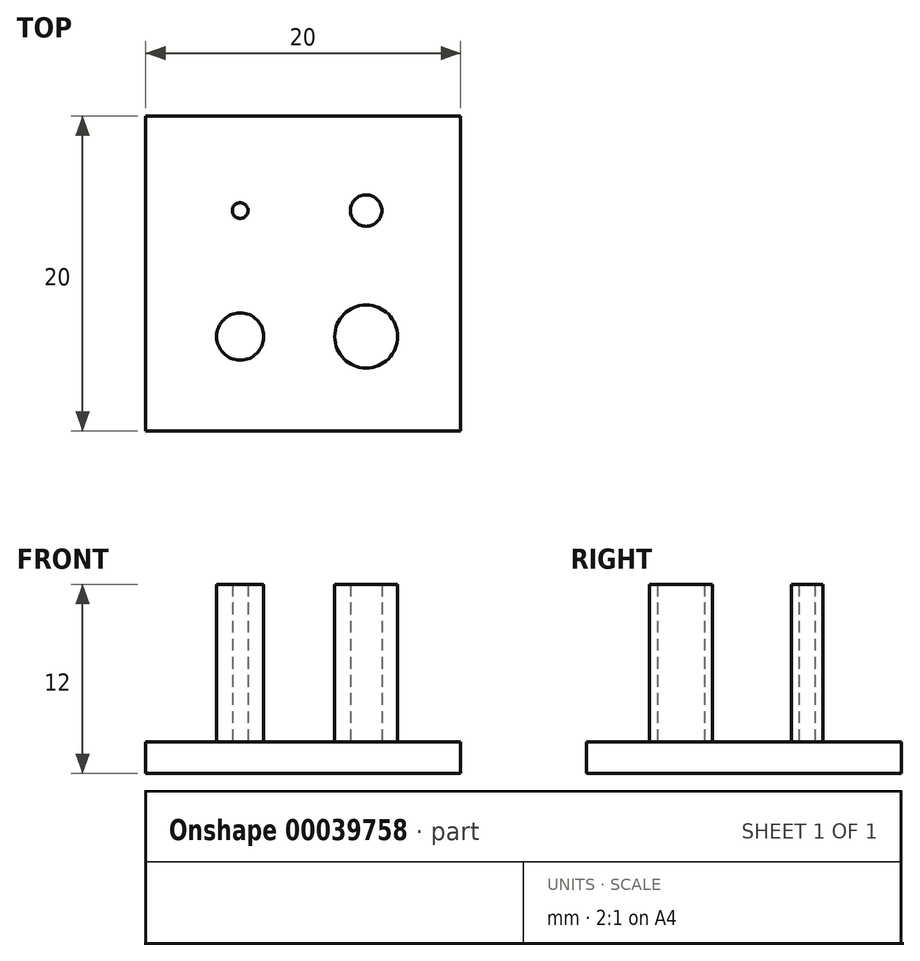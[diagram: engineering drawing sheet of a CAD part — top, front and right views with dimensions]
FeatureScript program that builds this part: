
annotation { "Feature Type Name" : "Feature", "Feature Type Description" : "" }
export const myFeature = defineFeature(function(context is Context, id is Id, definition is map)
    precondition{}
    {
        {
            var Q0;
            Q0=qCreatedBy(makeId("Top.planeOp"),FACE);
            var sketch = newSketch(context, id + "F0", { "sketchPlane" : qUnion([Q0])});
            skLineSegment(sketch, "E0.bottom", {"start": v(-20, 0) * mm, "end": v(0, 0) * mm});
            skLineSegment(sketch, "E0.top", {"start": v(-20, -20) * mm, "end": v(0, -20) * mm});
            skLineSegment(sketch, "E0.left", {"start": v(-20, 0) * mm, "end": v(-20, -20) * mm});
            skLineSegment(sketch, "E0.right", {"start": v(0, 0) * mm, "end": v(0, -20) * mm});
            skCircle(sketch, "E1", {"center": v(-14, -6) * mm, "radius": 0.5 * mm});
            skCircle(sketch, "E2", {"center": v(-6, -6) * mm, "radius": 1 * mm});
            skCircle(sketch, "E3", {"center": v(-14, -14) * mm, "radius": 1.5 * mm});
            skCircle(sketch, "E4", {"center": v(-6, -14) * mm, "radius": 2 * mm});
            skSolve(sketch);
        }
        {
            var Q0;
            Q0=makeQuery(id+"F0.imprint","IMPRINT",FACE,{"disambiguationData":[TD([[makeQuery(id+"F0.imprint","IMPRINT",EDGE,{"derivedFrom":sQuery(id+"F0.wireOp",EDGE,"E0.bottom")}),-1.0]])]});
            var Q1;
            Q1=makeQuery(id+"F0.imprint","IMPRINT",FACE,{"disambiguationData":[TD([[makeQuery(id+"F0.imprint","IMPRINT",EDGE,{"derivedFrom":sQuery(id+"F0.wireOp",EDGE,"E1")}),1.0]])]});
            var Q2;
            Q2=makeQuery(id+"F0.imprint","IMPRINT",FACE,{"disambiguationData":[TD([[makeQuery(id+"F0.imprint","IMPRINT",EDGE,{"derivedFrom":sQuery(id+"F0.wireOp",EDGE,"E2")}),1.0]])]});
            var Q3;
            Q3=makeQuery(id+"F0.imprint","IMPRINT",FACE,{"disambiguationData":[TD([[makeQuery(id+"F0.imprint","IMPRINT",EDGE,{"derivedFrom":sQuery(id+"F0.wireOp",EDGE,"E4")}),1.0]])]});
            var Q4;
            Q4=makeQuery(id+"F0.imprint","IMPRINT",FACE,{"disambiguationData":[TD([[makeQuery(id+"F0.imprint","IMPRINT",EDGE,{"derivedFrom":sQuery(id+"F0.wireOp",EDGE,"E3")}),1.0]])]});
            extrude(context, id + "F1", {"entities" : qUnion([Q0, Q1, Q2, Q3, Q4]), "depth" : 2 * mm});
        }
        {
            var Q0;
            Q0=makeQuery(id+"F1.opExtrude","CAP_FACE",FACE,{"disambiguationData":[OSD([sQuery(id+"F0.wireOp",EDGE,"E0.bottom"),sQuery(id+"F0.wireOp",EDGE,"E0.top"),sQuery(id+"F0.wireOp",EDGE,"E0.left"),sQuery(id+"F0.wireOp",EDGE,"E0.right")])],"isStart":false});
            var sketch = newSketch(context, id + "F2", { "sketchPlane" : qUnion([Q0])});
            skCircle(sketch, "E5.0", {"center": v(-6, -6) * mm, "radius": 1 * mm});
            skCircle(sketch, "E6.0", {"center": v(-14, -6) * mm, "radius": 0.5 * mm});
            skCircle(sketch, "E7.0", {"center": v(-14, -14) * mm, "radius": 1.5 * mm});
            skCircle(sketch, "E8.0", {"center": v(-6, -14) * mm, "radius": 2 * mm});
            skSolve(sketch);
        }
        {
            var Q0;
            Q0=makeQuery(id+"F2.imprint","IMPRINT",FACE,{"disambiguationData":[TD([[makeQuery(id+"F2.imprint","IMPRINT",EDGE,{"derivedFrom":sQuery(id+"F2.wireOp",EDGE,"E5.0")}),1.0]])]});
            var Q1;
            Q1=makeQuery(id+"F2.imprint","IMPRINT",FACE,{"disambiguationData":[TD([[makeQuery(id+"F2.imprint","IMPRINT",EDGE,{"derivedFrom":sQuery(id+"F2.wireOp",EDGE,"E6.0")}),1.0]])]});
            var Q2;
            Q2=makeQuery(id+"F2.imprint","IMPRINT",FACE,{"disambiguationData":[TD([[makeQuery(id+"F2.imprint","IMPRINT",EDGE,{"derivedFrom":sQuery(id+"F2.wireOp",EDGE,"E8.0")}),1.0]])]});
            var Q3;
            Q3=makeQuery(id+"F2.imprint","IMPRINT",FACE,{"disambiguationData":[TD([[makeQuery(id+"F2.imprint","IMPRINT",EDGE,{"derivedFrom":sQuery(id+"F2.wireOp",EDGE,"E7.0")}),1.0]])]});
            extrude(context, id + "F3", {"entities" : qUnion([Q0, Q1, Q2, Q3]), "operationType" : NewBodyOperationType.ADD, "depth" : 10 * mm});
        }
    });
